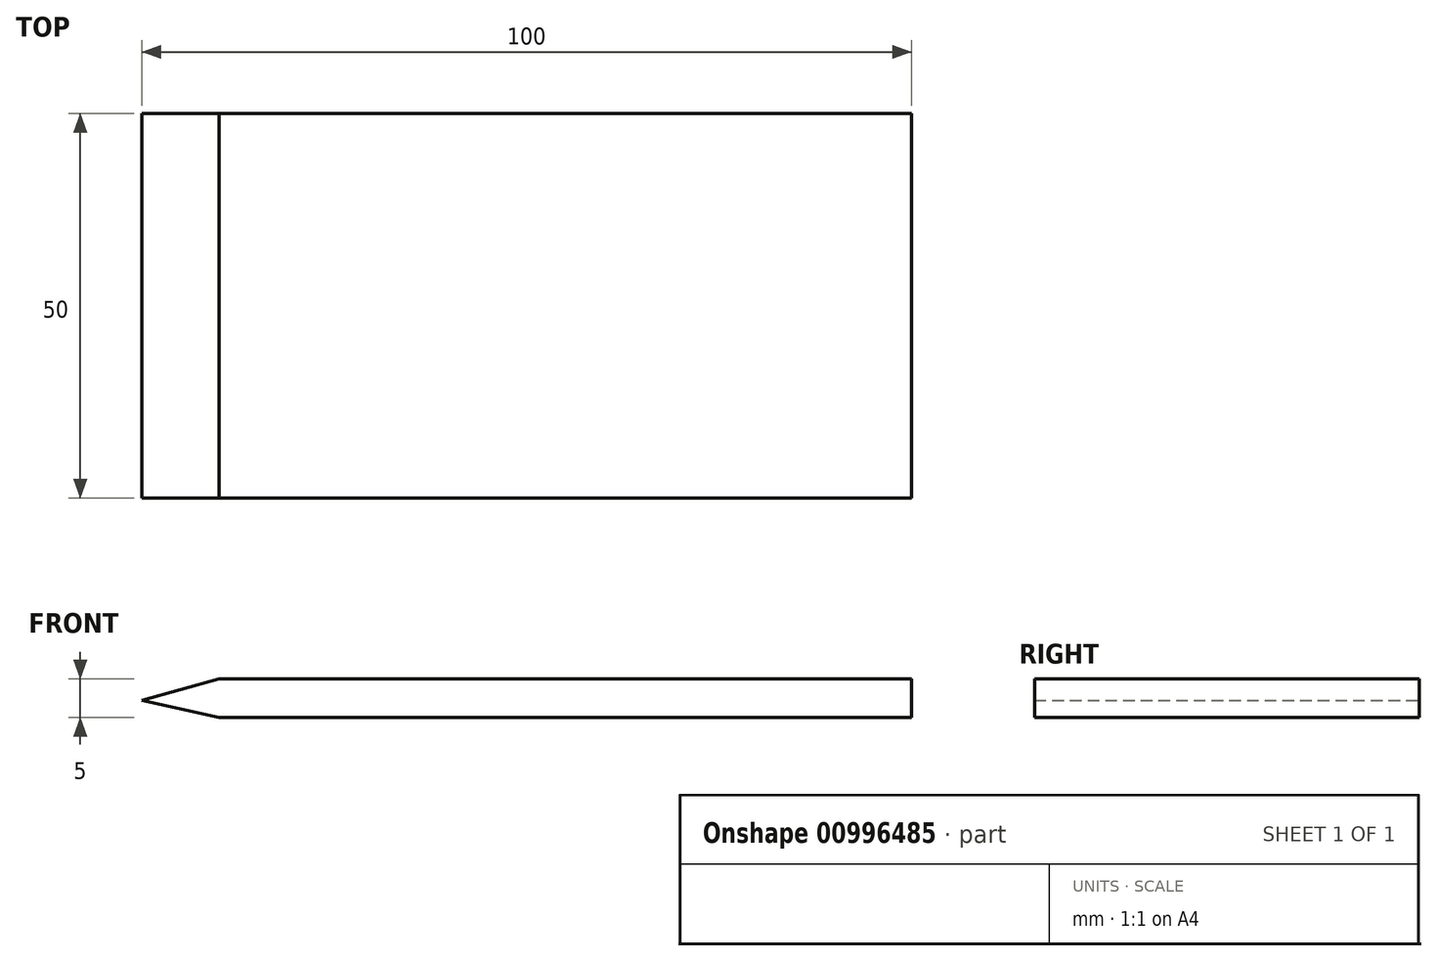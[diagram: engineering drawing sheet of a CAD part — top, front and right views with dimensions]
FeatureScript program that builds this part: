
annotation { "Feature Type Name" : "Feature", "Feature Type Description" : "" }
export const myFeature = defineFeature(function(context is Context, id is Id, definition is map)
    precondition{}
    {
        {
            var Q0;
            Q0=qCreatedBy(makeId("Front.planeOp"),FACE);
            var sketch = newSketch(context, id + "F0", { "sketchPlane" : qUnion([Q0])});
            skLineSegment(sketch, "E0", {"start": v(-45.22, 0) * mm, "end": v(44.78, 0) * mm});
            skLineSegment(sketch, "E1", {"start": v(-45.22, -5) * mm, "end": v(44.78, -5) * mm});
            skLineSegment(sketch, "E2", {"start": v(-55.22, -2.78) * mm, "end": v(-45.22, 0) * mm});
            skLineSegment(sketch, "E3", {"start": v(-45.22, -5) * mm, "end": v(-55.22, -2.78) * mm});
            skLineSegment(sketch, "E4", {"start": v(44.78, 0) * mm, "end": v(44.78, -5) * mm});
            skSolve(sketch);
        }
        {
            var Q0;
            Q0=makeQuery(id+"F0.imprint","IMPRINT",FACE,{"disambiguationData":[TD([[makeQuery(id+"F0.imprint","IMPRINT",EDGE,{"derivedFrom":sQuery(id+"F0.wireOp",EDGE,"E0")}),-1.0]])]});
            extrude(context, id + "F1", {"entities" : qUnion([Q0]), "endBound" : BoundingType.SYMMETRIC, "depth" : 50 * mm, "offsetDistance" : 25 * mm});
        }
    });
